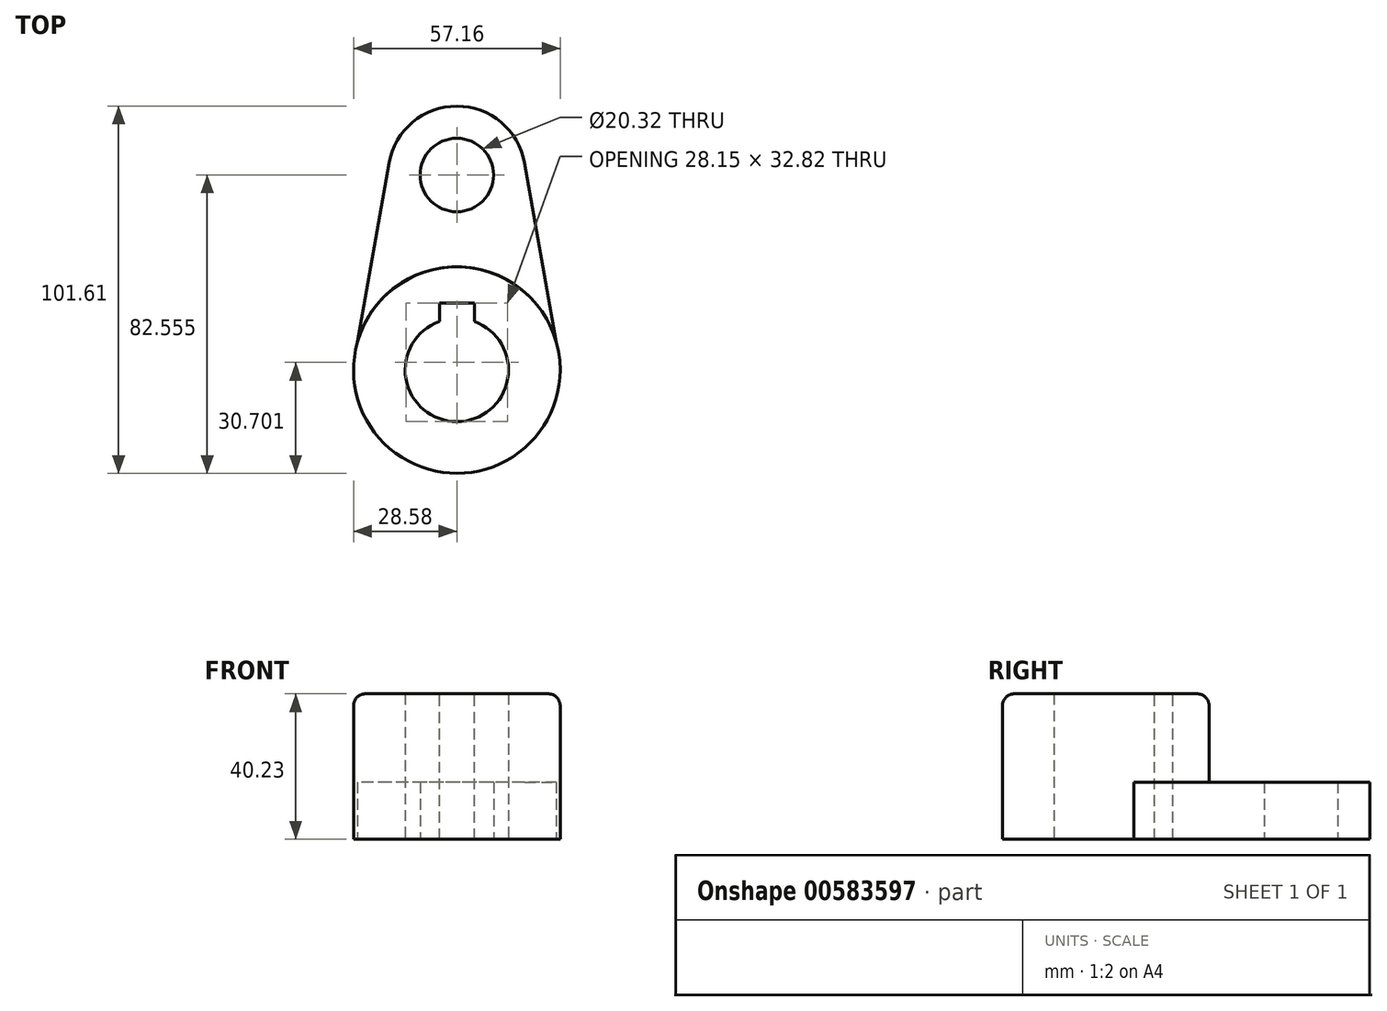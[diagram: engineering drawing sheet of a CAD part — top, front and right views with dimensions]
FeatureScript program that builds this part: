
annotation { "Feature Type Name" : "Feature", "Feature Type Description" : "" }
export const myFeature = defineFeature(function(context is Context, id is Id, definition is map)
    precondition{}
    {
        {
            var Q0;
            Q0=qCreatedBy(makeId("Top.planeOp"),FACE);
            var sketch = newSketch(context, id + "F0", { "sketchPlane" : qUnion([Q0])});
            skCircle(sketch, "E0", {"center": v(0, 0) * mm, "radius": 28.58 * mm});
            skCircle(sketch, "E1", {"center": v(0, 0) * mm, "radius": 14.29 * mm});
            skLineSegment(sketch, "E2", {"start": v(-4.83, 18.53) * mm, "end": v(4.83, 18.53) * mm});
            skPoint(sketch, "E3", {"position": v(0, 18.53) * mm});
            skSolve(sketch);
        }
        {
            var Q0;
            Q0 = qSketchRegion(id + "F0", true);
            extrude(context, id + "F1", {"entities" : qUnion([Q0]), "depth" : 40.23 * mm, "offsetDistance" : 25.4 * mm});
        }
        {
            var Q0;
            Q0=makeQuery(id+"F1.opExtrude","CAP_FACE",FACE,{"disambiguationData":[OSD([sQuery(id+"F0.wireOp",EDGE,"E0"),sQuery(id+"F0.wireOp",EDGE,"E1")])],"isStart":false});
            var sketch = newSketch(context, id + "F2", { "sketchPlane" : qUnion([Q0])});
            skLineSegment(sketch, "E4", {"start": v(-4.83, 18.53) * mm, "end": v(4.83, 18.53) * mm});
            skPoint(sketch, "E5", {"position": v(0, 18.53) * mm});
            skLineSegment(sketch, "E6", {"start": v(-4.83, 18.53) * mm, "end": v(-4.83, 13.45) * mm});
            skLineSegment(sketch, "E7", {"start": v(-4.83, 13.45) * mm, "end": v(4.83, 13.45) * mm});
            skLineSegment(sketch, "E8", {"start": v(4.83, 13.45) * mm, "end": v(4.83, 18.53) * mm});
            skSolve(sketch);
        }
        {
            var Q0;
            Q0 = qSketchRegion(id + "F2", true);
            extrude(context, id + "F3", {"entities" : qUnion([Q0]), "operationType" : NewBodyOperationType.REMOVE, "endBound" : BoundingType.THROUGH_ALL, "oppositeDirection" : true, "depth" : 25.4 * mm, "offsetDistance" : 25.4 * mm});
        }
        {
            var Q0;
            Q0=qCreatedBy(makeId("Top.planeOp"),FACE);
            var sketch = newSketch(context, id + "F4", { "sketchPlane" : qUnion([Q0])});
            skPoint(sketch, "E9", {"position": v(0, 53.97) * mm});
            skCircle(sketch, "E10", {"center": v(0, 53.97) * mm, "radius": 10.16 * mm});
            skPoint(sketch, "E11", {"position": v(0, 73.03) * mm});
            skLineSegment(sketch, "E12", {"start": v(-18.76, 57.29) * mm, "end": v(-28.35, 2.93) * mm});
            skLineSegment(sketch, "E13", {"start": v(18.76, 57.29) * mm, "end": v(28.35, 2.93) * mm});
            skArc(sketch, "E14", {"start": v(-18.76, 57.29) * mm, "mid": v(0, 73.02) * mm, "end": v(18.76, 57.29) * mm});
            skCircle(sketch, "E15", {"center": v(0, 0) * mm, "radius": 28.5 * mm});
            skSolve(sketch);
        }
        {
            var Q0;
            Q0=makeQuery(id+"F4.imprint","IMPRINT",FACE,{"disambiguationData":[TD([[makeQuery(id+"F4.imprint","IMPRINT",EDGE,{"derivedFrom":sQuery(id+"F4.wireOp",EDGE,"E10")}),-1.0]])]});
            extrude(context, id + "F5", {"entities" : qUnion([Q0]), "operationType" : NewBodyOperationType.ADD, "depth" : 15.77 * mm, "offsetDistance" : 25.4 * mm});
        }
        {
            var Q0;
            Q0=makeQuery(id+"F1.opExtrude","CAP_EDGE",EDGE,{"disambiguationData":[OSD([sQuery(id+"F0.wireOp",EDGE,"E0")])],"isStart":false});
            fillet(context, id + "F6", {"entities" : qUnion([Q0]), "radius" : 3.3 * mm, "tangentPropagation" : true, "allowEdgeOverflow" : false});
        }
    });
